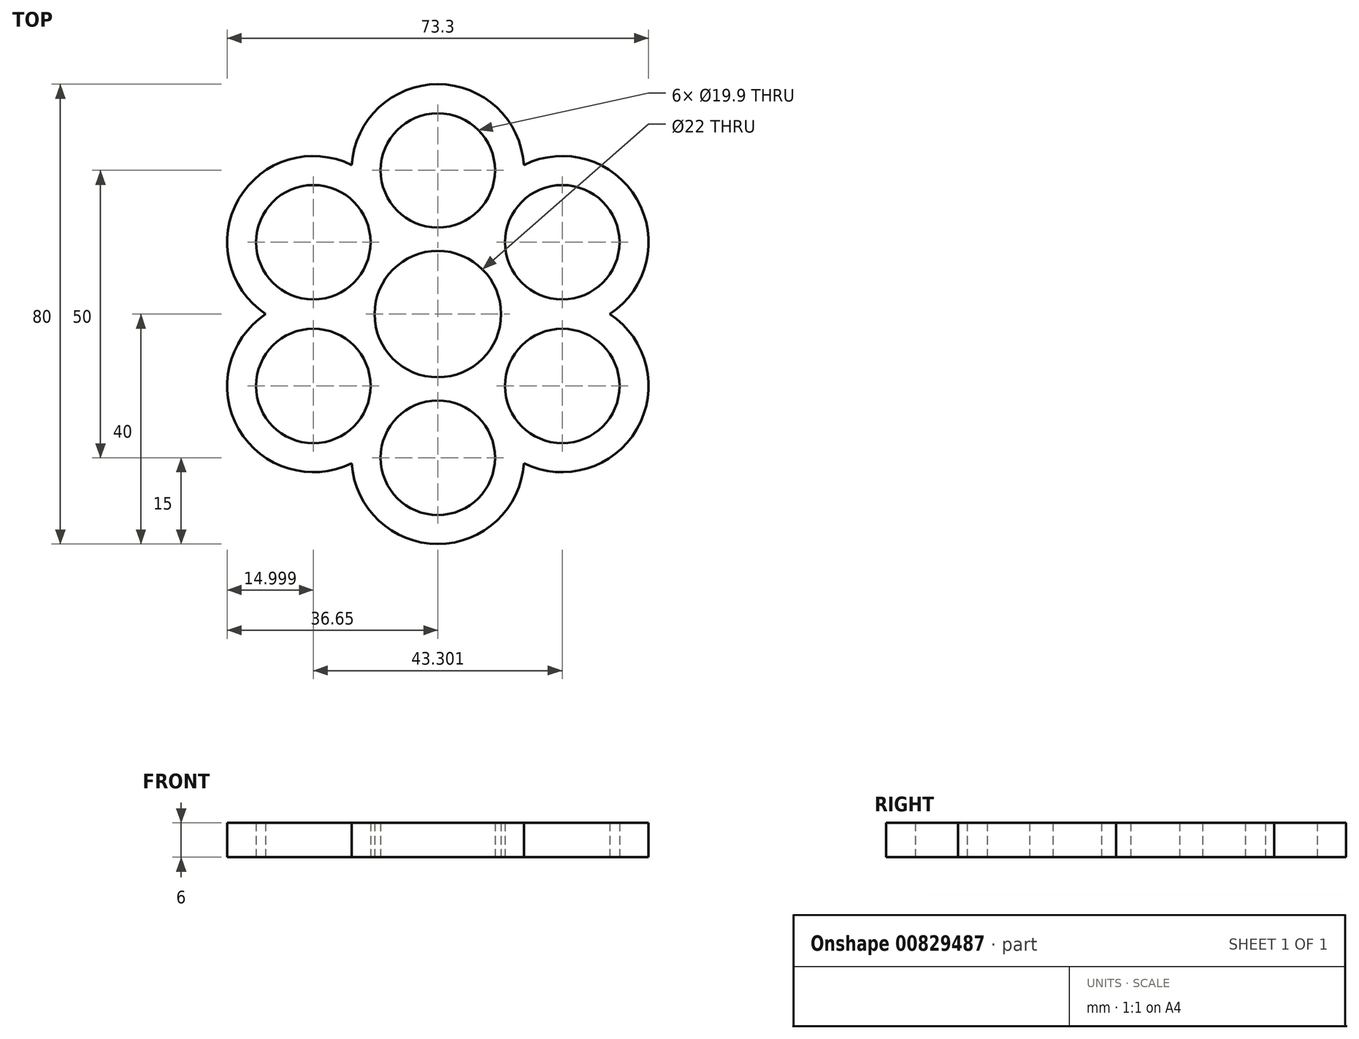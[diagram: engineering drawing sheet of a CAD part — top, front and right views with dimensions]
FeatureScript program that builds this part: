
annotation { "Feature Type Name" : "Feature", "Feature Type Description" : "" }
export const myFeature = defineFeature(function(context is Context, id is Id, definition is map)
    precondition{}
    {
        {
            var Q0;
            Q0=qCreatedBy(makeId("Top.planeOp"),FACE);
            var sketch = newSketch(context, id + "F0", { "sketchPlane" : qUnion([Q0])});
            skArc(sketch, "E0", {"start": v(5.5, 9.53) * mm, "mid": v(0, 11) * mm, "end": v(-5.5, 9.53) * mm});
            skCircle(sketch, "E1", {"center": v(0, 25) * mm, "radius": 9.95 * mm});
            skArc(sketch, "E2", {"start": v(14.97, 25.93) * mm, "mid": v(0, 40) * mm, "end": v(-14.97, 25.93) * mm});
            skArc(sketch, "E3.1.0", {"start": v(-5.5, 9.53) * mm, "mid": v(-9.53, 5.5) * mm, "end": v(-11, 0) * mm});
            skCircle(sketch, "E3.1.1", {"center": v(-21.65, 12.5) * mm, "radius": 9.95 * mm});
            skArc(sketch, "E3.1.2", {"start": v(-14.97, 25.93) * mm, "mid": v(-34.64, 20) * mm, "end": v(-29.94, 0) * mm});
            skArc(sketch, "E3.2.0", {"start": v(-11, 0) * mm, "mid": v(-9.53, -5.5) * mm, "end": v(-5.5, -9.53) * mm});
            skCircle(sketch, "E3.2.1", {"center": v(-21.65, -12.5) * mm, "radius": 9.95 * mm});
            skArc(sketch, "E3.2.2", {"start": v(-29.94, 0) * mm, "mid": v(-34.64, -20) * mm, "end": v(-14.97, -25.93) * mm});
            skArc(sketch, "E3.3.0", {"start": v(-5.5, -9.53) * mm, "mid": v(0, -11) * mm, "end": v(5.5, -9.53) * mm});
            skCircle(sketch, "E3.3.1", {"center": v(0, -25) * mm, "radius": 9.95 * mm});
            skArc(sketch, "E3.3.2", {"start": v(-14.97, -25.93) * mm, "mid": v(0, -40) * mm, "end": v(14.97, -25.93) * mm});
            skArc(sketch, "E3.4.0", {"start": v(5.5, -9.53) * mm, "mid": v(9.53, -5.5) * mm, "end": v(11, 0) * mm});
            skCircle(sketch, "E3.4.1", {"center": v(21.65, -12.5) * mm, "radius": 9.95 * mm});
            skArc(sketch, "E3.4.2", {"start": v(14.97, -25.93) * mm, "mid": v(34.64, -20) * mm, "end": v(29.94, 0) * mm});
            skArc(sketch, "E3.5.0", {"start": v(11, 0) * mm, "mid": v(9.53, 5.5) * mm, "end": v(5.5, 9.53) * mm});
            skCircle(sketch, "E3.5.1", {"center": v(21.65, 12.5) * mm, "radius": 9.95 * mm});
            skArc(sketch, "E3.5.2", {"start": v(29.94, 0) * mm, "mid": v(34.64, 20) * mm, "end": v(14.97, 25.93) * mm});
            skSolve(sketch);
        }
        {
            var Q0;
            Q0 = qSketchRegion(id + "F0", true);
            extrude(context, id + "F1", {"entities" : qUnion([Q0]), "depth" : 6 * mm, "offsetDistance" : 25 * mm});
        }
    });
